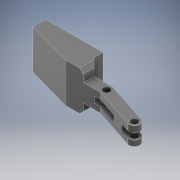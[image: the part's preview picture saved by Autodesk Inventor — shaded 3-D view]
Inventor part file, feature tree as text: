
AUTODESK INVENTOR PART (.ipt)
format: ipt  version: 2021 (Build 250183000, 183)  size: 188,416 bytes
history: native  units: mm
features: extrude x4, sketch x4, chamfer x3
ambient origin geometry x8: Origin, YZ Plane, XZ Plane, XY Plane, X Axis, Y Axis, Z Axis, Center Point
bodies: Solid1 (feature_tree)
feature tree (11):
  extrude  "Extrusion1"  Depth=6.0mm
  chamfer  "Chamfer1"  Distance=10.0mm
  chamfer  "Chamfer2"  Distance=45.0mm
  extrude  "Extrusion2"  Depth=35.0mm
  extrude  "Extrusion3"  Depth=7.0mm TaperAngle=45.0deg
  chamfer  "Chamfer3"  Distance=3.0mm Angle=45.0deg
  extrude  "Extrusion4"  Depth=6.0mm TaperAngle=0.0deg
  sketch  "Sketch1"  dims[d0=6.0mm d1=4.0mm]
  sketch  "Sketch3"  dims[d2=4.0mm d5=10.0mm d6=0.0mm]
  sketch  "Sketch4"  dims[d7=7.5mm]
  sketch  "Sketch5"  dims[d8=23.0mm d11=45.0mm d12=35.0mm d15=7.0mm d16=25.0mm d17=45.0deg d18=3.0mm d19=25.0mm d20=45.0deg d21=6.0mm d22=16.0mm d23=0.0mm d24=0.0mm d26=3.0mm d27=3.5mm d28=3.5mm d29=8.0mm d30=15.0mm d31=30.0mm d32=0.0mm d33=0.0mm d34=2.0mm d35=2.0mm d36=45.0deg d37=5.0mm d38=0.0mm d39=3.0mm]
